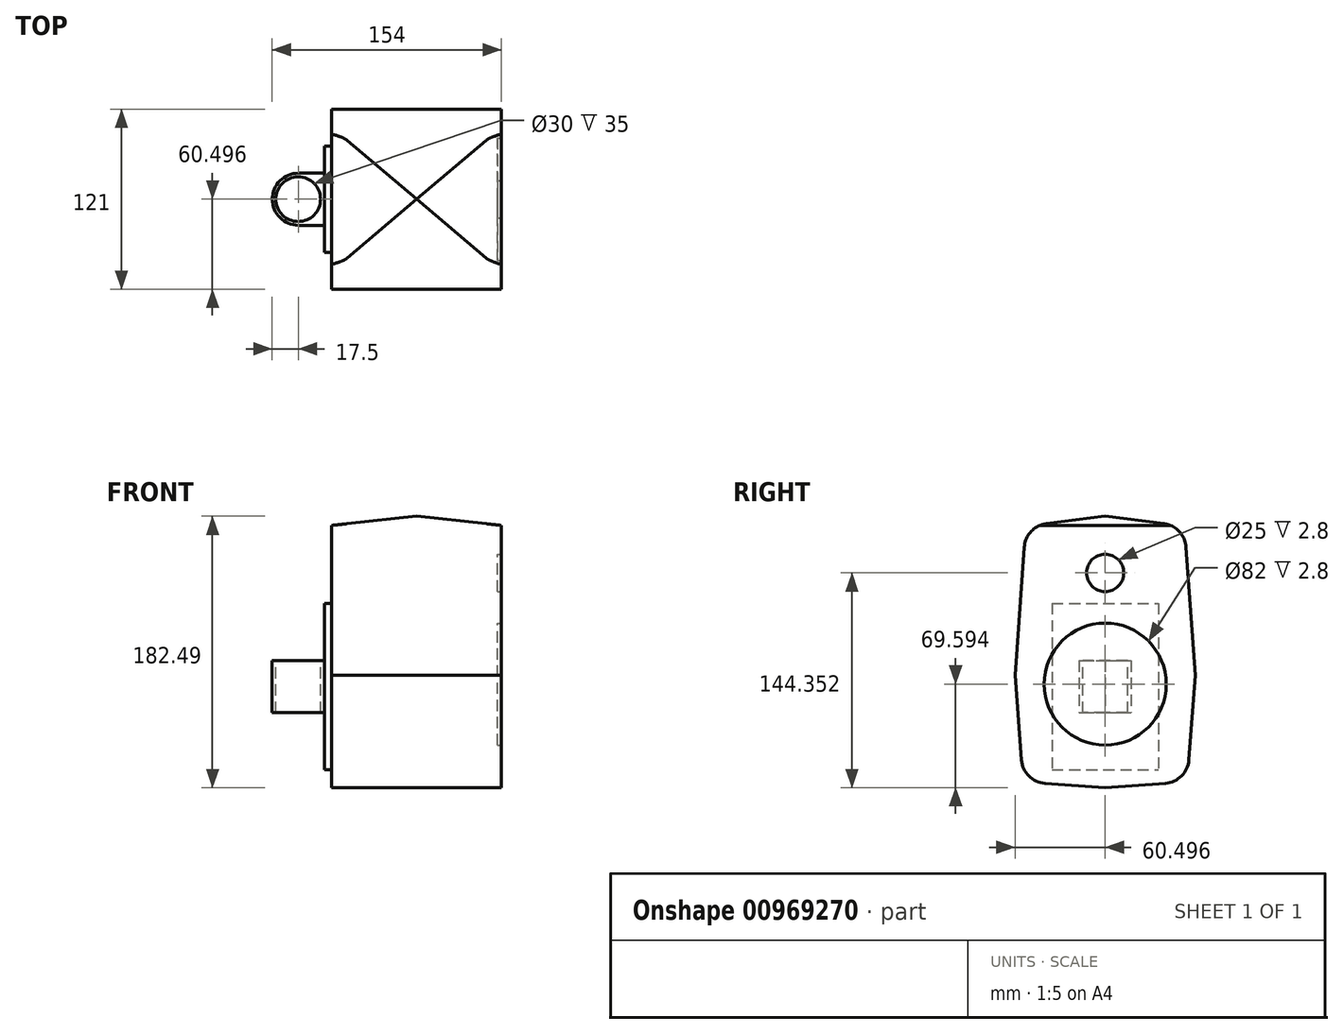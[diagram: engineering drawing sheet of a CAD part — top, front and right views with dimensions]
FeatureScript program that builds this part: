
annotation { "Feature Type Name" : "Feature", "Feature Type Description" : "" }
export const myFeature = defineFeature(function(context is Context, id is Id, definition is map)
    precondition{}
    {
        {
            var Q0;
            Q0=qCreatedBy(makeId("Right.planeOp"),FACE);
            var sketch = newSketch(context, id + "F0", { "sketchPlane" : qUnion([Q0])});
            skLineSegment(sketch, "E0.bottom", {"start": v(-67.51, 132.87) * mm, "end": v(53.49, 132.87) * mm});
            skLineSegment(sketch, "E0.top", {"start": v(-67.51, -62.13) * mm, "end": v(53.49, -62.13) * mm});
            skLineSegment(sketch, "E0.left", {"start": v(-67.51, 132.87) * mm, "end": v(-67.51, -62.13) * mm});
            skLineSegment(sketch, "E0.right", {"start": v(53.49, 132.87) * mm, "end": v(53.49, -62.13) * mm});
            skSolve(sketch);
        }
        {
            var Q0;
            Q0=makeQuery(id+"F0.imprint","IMPRINT",FACE,{"disambiguationData":[TD([[makeQuery(id+"F0.imprint","IMPRINT",EDGE,{"derivedFrom":sQuery(id+"F0.wireOp",EDGE,"E0.bottom")}),-1.0]])]});
            extrude(context, id + "F1", {"entities" : qUnion([Q0]), "depth" : 114 * mm, "offsetDistance" : 25 * mm});
        }
        {
            var Q0;
            Q0=makeQuery(id+"F1.opExtrude","CAP_FACE",FACE,{"disambiguationData":[OSD([sQuery(id+"F0.wireOp",EDGE,"E0.bottom"),sQuery(id+"F0.wireOp",EDGE,"E0.top"),sQuery(id+"F0.wireOp",EDGE,"E0.left"),sQuery(id+"F0.wireOp",EDGE,"E0.right")])],"isStart":false});
            var sketch = newSketch(context, id + "F2", { "sketchPlane" : qUnion([Q0])});
            skLineSegment(sketch, "E1", {"start": v(-7.01, 132.87) * mm, "end": v(-7.01, -62.13) * mm, "construction": true});
            skLineSegment(sketch, "E2", {"start": v(-7.01, 132.87) * mm, "end": v(-60.3, 126) * mm});
            skLineSegment(sketch, "E3", {"start": v(-7.01, -49.62) * mm, "end": v(-62.1, -45.64) * mm});
            skLineSegment(sketch, "E4", {"start": v(-62.1, -45.64) * mm, "end": v(-67.51, 26.1) * mm});
            skLineSegment(sketch, "E5", {"start": v(-67.51, 26.1) * mm, "end": v(-60.3, 126) * mm});
            skLineSegment(sketch, "E6.MirrorCS", {"start": v(-7.01, 132.87) * mm, "end": v(46.26, 126) * mm});
            skLineSegment(sketch, "E7.MirrorCS", {"start": v(53.49, 26.1) * mm, "end": v(46.26, 126) * mm});
            skLineSegment(sketch, "E8.MirrorCS", {"start": v(48.07, -45.64) * mm, "end": v(53.49, 26.1) * mm});
            skLineSegment(sketch, "E9.MirrorCS", {"start": v(-7.01, -49.62) * mm, "end": v(48.07, -45.64) * mm});
            skCircle(sketch, "E10", {"center": v(-7.01, 19.97) * mm, "radius": 41 * mm});
            skCircle(sketch, "E11", {"center": v(-7.01, 94.73) * mm, "radius": 12.5 * mm});
            skSolve(sketch);
        }
        {
            var Q0;
            {var subQ0=sQuery(id+"F2.wireOp",EDGE,"E2");Q0=makeQuery(id+"F2.imprint","IMPRINT",FACE,{"disambiguationData":[TD([[makeQuery(id+"F2.imprint","IMPRINT",EDGE,{"derivedFrom":subQ0}),-1.0]])]});}
            var Q1;
            {var subQ0=sQuery(id+"F2.wireOp",EDGE,"E6.MirrorCS");Q1=makeQuery(id+"F2.imprint","IMPRINT",FACE,{"disambiguationData":[TD([[makeQuery(id+"F2.imprint","IMPRINT",EDGE,{"derivedFrom":subQ0}),1.0]])]});}
            var Q2;
            Q2=makeQuery(id+"F2.imprint","IMPRINT",FACE,{"disambiguationData":[TD([[makeQuery(id+"F2.imprint","IMPRINT",EDGE,{"derivedFrom":sQuery(id+"F2.wireOp",EDGE,"E3")}),1.0]])]});
            extrude(context, id + "F3", {"entities" : qUnion([Q0, Q1, Q2]), "operationType" : NewBodyOperationType.REMOVE, "endBound" : BoundingType.UP_TO_NEXT, "oppositeDirection" : true, "depth" : 25 * mm, "offsetDistance" : 25 * mm});
        }
        {
            var Q0;
            Q0=makeQuery(id+"F3.boolean.opBoolean","COPY",EDGE,{"derivedFrom":makeQuery(id+"F3.opExtrude","SWEPT_EDGE",EDGE,{"disambiguationData":[OSD([sQuery(id+"F2.wireOp",EDGE,"E2"),sQuery(id+"F2.wireOp",EDGE,"E5")])]})});
            var Q1;
            Q1=makeQuery(id+"F3.boolean.opBoolean","COPY",EDGE,{"derivedFrom":makeQuery(id+"F3.opExtrude","SWEPT_EDGE",EDGE,{"disambiguationData":[OSD([sQuery(id+"F2.wireOp",EDGE,"E6.MirrorCS"),sQuery(id+"F2.wireOp",EDGE,"E7.MirrorCS")])]})});
            var Q2;
            Q2=makeQuery(id+"F3.boolean.opBoolean","COPY",EDGE,{"derivedFrom":makeQuery(id+"F3.opExtrude","SWEPT_EDGE",EDGE,{"disambiguationData":[OSD([sQuery(id+"F2.wireOp",EDGE,"E8.MirrorCS"),sQuery(id+"F2.wireOp",EDGE,"E9.MirrorCS")])]})});
            var Q3;
            Q3=makeQuery(id+"F3.boolean.opBoolean","COPY",EDGE,{"derivedFrom":makeQuery(id+"F3.opExtrude","SWEPT_EDGE",EDGE,{"disambiguationData":[OSD([sQuery(id+"F2.wireOp",EDGE,"E3"),sQuery(id+"F2.wireOp",EDGE,"E4")])]})});
            fillet(context, id + "F4", {"entities" : qUnion([Q0, Q1, Q2, Q3]), "radius" : 17 * mm, "tangentPropagation" : true, "allowEdgeOverflow" : false});
        }
        {
            var Q0;
            Q0=qCreatedBy(makeId("Front.planeOp"),FACE);
            var sketch = newSketch(context, id + "F5", { "sketchPlane" : qUnion([Q0])});
            skLineSegment(sketch, "E12.0", {"start": v(0, 132.87) * mm, "end": v(114, 132.87) * mm});
            skLineSegment(sketch, "E13.0", {"start": v(0, -49.62) * mm, "end": v(114, -49.62) * mm});
            skLineSegment(sketch, "E14", {"start": v(57, 132.87) * mm, "end": v(0, 126.65) * mm});
            skLineSegment(sketch, "E15", {"start": v(57, 132.87) * mm, "end": v(114, 126.65) * mm});
            skLineSegment(sketch, "E16", {"start": v(114, 126.65) * mm, "end": v(114, 132.87) * mm});
            skLineSegment(sketch, "E17", {"start": v(0, 126.65) * mm, "end": v(0, 132.87) * mm});
            skSolve(sketch);
        }
        {
            var Q0;
            {var subQ2=sQuery(id+"F5.wireOp",EDGE,"E14");Q0=makeQuery(id+"F5.imprint","IMPRINT",FACE,{"disambiguationData":[TD([[makeQuery(id+"F5.imprint","IMPRINT",EDGE,{"derivedFrom":subQ2}),-1.0]])]});}
            var Q1;
            {var subQ2=sQuery(id+"F5.wireOp",EDGE,"E15");Q1=makeQuery(id+"F5.imprint","IMPRINT",FACE,{"disambiguationData":[TD([[makeQuery(id+"F5.imprint","IMPRINT",EDGE,{"derivedFrom":subQ2}),1.0]])]});}
            extrude(context, id + "F6", {"entities" : qUnion([Q0, Q1]), "operationType" : NewBodyOperationType.REMOVE, "oppositeDirection" : true, "depth" : 134.1 * mm, "offsetDistance" : 25 * mm});
        }
        {
            var Q0;
            {var subQ2=sQuery(id+"F5.wireOp",EDGE,"E14");Q0=makeQuery(id+"F5.imprint","IMPRINT",FACE,{"disambiguationData":[TD([[makeQuery(id+"F5.imprint","IMPRINT",EDGE,{"derivedFrom":subQ2}),-1.0]])]});}
            var Q1;
            {var subQ2=sQuery(id+"F5.wireOp",EDGE,"E15");Q1=makeQuery(id+"F5.imprint","IMPRINT",FACE,{"disambiguationData":[TD([[makeQuery(id+"F5.imprint","IMPRINT",EDGE,{"derivedFrom":subQ2}),1.0]])]});}
            extrude(context, id + "F7", {"entities" : qUnion([Q0, Q1]), "operationType" : NewBodyOperationType.REMOVE, "depth" : 135.6 * mm, "offsetDistance" : 25 * mm});
        }
        {
            var Q0;
            Q0=makeQuery(id+"F2.imprint","IMPRINT",FACE,{"disambiguationData":[TD([[makeQuery(id+"F2.imprint","IMPRINT",EDGE,{"derivedFrom":sQuery(id+"F2.wireOp",EDGE,"E10")}),1.0]])]});
            var Q1;
            Q1=makeQuery(id+"F2.imprint","IMPRINT",FACE,{"disambiguationData":[TD([[makeQuery(id+"F2.imprint","IMPRINT",EDGE,{"derivedFrom":sQuery(id+"F2.wireOp",EDGE,"E11")}),1.0]])]});
            extrude(context, id + "F8", {"entities" : qUnion([Q0, Q1]), "operationType" : NewBodyOperationType.REMOVE, "oppositeDirection" : true, "depth" : 2.8 * mm, "offsetDistance" : 25 * mm});
        }
        {
            var Q0;
            Q0=makeQuery(id+"F1.opExtrude","CAP_FACE",FACE,{"disambiguationData":[OSD([sQuery(id+"F0.wireOp",EDGE,"E0.bottom"),sQuery(id+"F0.wireOp",EDGE,"E0.top"),sQuery(id+"F0.wireOp",EDGE,"E0.left"),sQuery(id+"F0.wireOp",EDGE,"E0.right")])],"isStart":true});
            var sketch = newSketch(context, id + "F9", { "sketchPlane" : qUnion([Q0])});
            skLineSegment(sketch, "E18", {"start": v(7.01, 126.65) * mm, "end": v(7.01, -49.62) * mm, "construction": true});
            skLineSegment(sketch, "E19.bottom", {"start": v(42.76, 74.32) * mm, "end": v(-28.74, 74.32) * mm});
            skLineSegment(sketch, "E19.top", {"start": v(42.76, -37.67) * mm, "end": v(-28.74, -37.67) * mm});
            skLineSegment(sketch, "E19.left", {"start": v(42.76, 74.32) * mm, "end": v(42.76, -37.67) * mm});
            skLineSegment(sketch, "E19.right", {"start": v(-28.74, 74.32) * mm, "end": v(-28.74, -37.67) * mm});
            skPoint(sketch, "E19.middle", {"position": v(7.01, 18.33) * mm});
            skSolve(sketch);
        }
        {
            var Q0;
            Q0 = qSketchRegion(id + "F9", true);
            extrude(context, id + "F10", {"entities" : qUnion([Q0]), "operationType" : NewBodyOperationType.ADD, "depth" : 5 * mm, "offsetDistance" : 25 * mm});
        }
        {
            var Q0;
            Q0=makeQuery(id+"F10.opExtrude","CAP_FACE",FACE,{"disambiguationData":[OSD([sQuery(id+"F9.wireOp",EDGE,"E19.bottom"),sQuery(id+"F9.wireOp",EDGE,"E19.top"),sQuery(id+"F9.wireOp",EDGE,"E19.left"),sQuery(id+"F9.wireOp",EDGE,"E19.right")])],"isStart":false});
            var sketch = newSketch(context, id + "F11", { "sketchPlane" : qUnion([Q0])});
            skLineSegment(sketch, "E20", {"start": v(-28.74, 74.32) * mm, "end": v(42.76, -37.67) * mm, "construction": true});
            skLineSegment(sketch, "E21", {"start": v(42.76, 74.32) * mm, "end": v(-28.74, -37.67) * mm, "construction": true});
            skLineSegment(sketch, "E22.bottom", {"start": v(24.51, 35.83) * mm, "end": v(-10.49, 35.83) * mm});
            skLineSegment(sketch, "E22.top", {"start": v(24.51, 0.83) * mm, "end": v(-10.49, 0.83) * mm});
            skLineSegment(sketch, "E22.left", {"start": v(24.51, 35.83) * mm, "end": v(24.51, 0.83) * mm});
            skLineSegment(sketch, "E22.right", {"start": v(-10.49, 35.83) * mm, "end": v(-10.49, 0.83) * mm});
            skPoint(sketch, "E22.middle", {"position": v(7.01, 18.33) * mm});
            skSolve(sketch);
        }
        {
            var Q0;
            Q0=makeQuery(id+"F11.imprint","IMPRINT",FACE,{"disambiguationData":[TD([[makeQuery(id+"F11.imprint","IMPRINT",EDGE,{"derivedFrom":sQuery(id+"F11.wireOp",EDGE,"E22.bottom")}),1.0]])]});
            extrude(context, id + "F12", {"entities" : qUnion([Q0]), "operationType" : NewBodyOperationType.ADD, "depth" : 35 * mm, "offsetDistance" : 25 * mm});
        }
        {
            var Q0;
            Q0=makeQuery(id+"F12.opExtrude","SWEPT_FACE",FACE,{"disambiguationData":[OSD([sQuery(id+"F11.wireOp",EDGE,"E22.bottom")])]});
            var sketch = newSketch(context, id + "F13", { "sketchPlane" : qUnion([Q0])});
            skLineSegment(sketch, "E23", {"start": v(-40, 10.49) * mm, "end": v(-5, -24.51) * mm, "construction": true});
            skLineSegment(sketch, "E24", {"start": v(-5, 10.49) * mm, "end": v(-40, -24.51) * mm, "construction": true});
            skCircle(sketch, "E25", {"center": v(-22.5, -7.01) * mm, "radius": 15 * mm});
            skSolve(sketch);
        }
        {
            var Q0;
            Q0=makeQuery(id+"F13.imprint","IMPRINT",FACE,{"disambiguationData":[TD([[makeQuery(id+"F13.imprint","IMPRINT",EDGE,{"derivedFrom":sQuery(id+"F13.wireOp",EDGE,"E25")}),1.0]])]});
            extrude(context, id + "F14", {"entities" : qUnion([Q0]), "operationType" : NewBodyOperationType.REMOVE, "endBound" : BoundingType.UP_TO_NEXT, "oppositeDirection" : true, "depth" : 25 * mm, "offsetDistance" : 25 * mm});
        }
        {
            var Q0;
            Q0=makeQuery(id+"F12.opExtrude","CAP_EDGE",EDGE,{"disambiguationData":[OSD([sQuery(id+"F11.wireOp",EDGE,"E22.left")])],"isStart":false});
            var Q1;
            Q1=makeQuery(id+"F12.opExtrude","CAP_EDGE",EDGE,{"disambiguationData":[OSD([sQuery(id+"F11.wireOp",EDGE,"E22.right")])],"isStart":false});
            fillet(context, id + "F15", {"entities" : qUnion([Q0, Q1]), "radius" : 17.62 * mm, "tangentPropagation" : true, "allowEdgeOverflow" : false});
        }
    });
